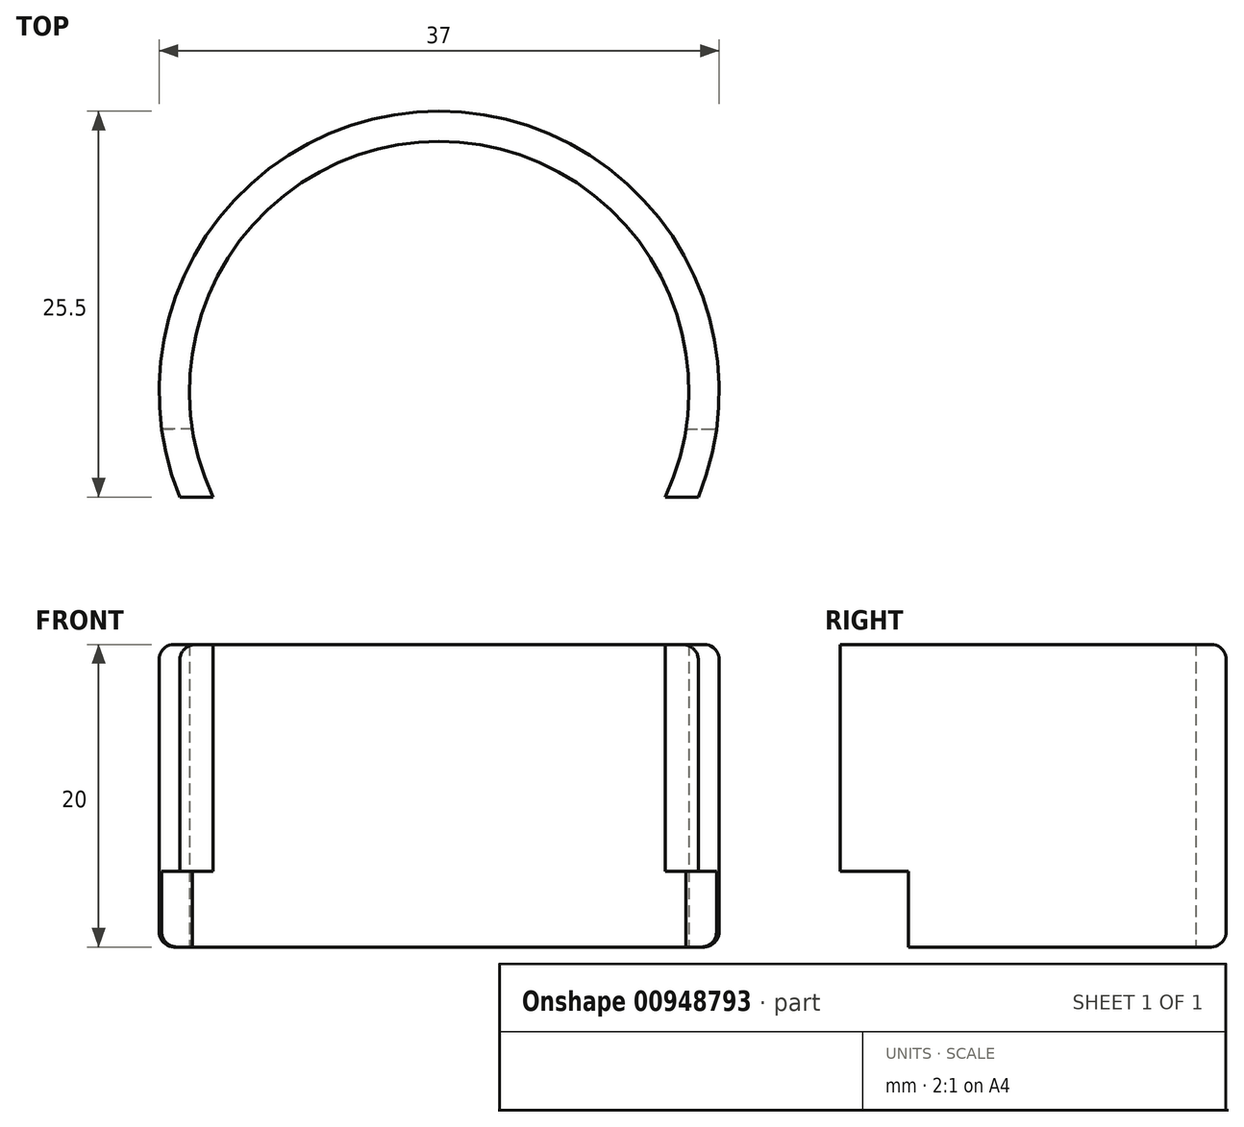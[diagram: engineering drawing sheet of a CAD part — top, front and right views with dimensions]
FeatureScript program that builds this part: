
annotation { "Feature Type Name" : "Feature", "Feature Type Description" : "" }
export const myFeature = defineFeature(function(context is Context, id is Id, definition is map)
    precondition{}
    {
        {
            var Q0;
            Q0=qCreatedBy(makeId("Top.planeOp"),FACE);
            var sketch = newSketch(context, id + "F0", { "sketchPlane" : qUnion([Q0])});
            skCircle(sketch, "E0", {"center": v(0, 0) * mm, "radius": 16.5 * mm});
            skCircle(sketch, "E1", {"center": v(0, 0) * mm, "radius": 18.5 * mm});
            skLineSegment(sketch, "E2", {"start": v(0, 0) * mm, "end": v(0, -7) * mm});
            skLineSegment(sketch, "E3", {"start": v(0, -7) * mm, "end": v(25.6, -7) * mm});
            skLineSegment(sketch, "E4", {"start": v(0, -7) * mm, "end": v(-26.93, -7) * mm});
            skPoint(sketch, "E5", {"position": v(0, -2.5) * mm});
            skLineSegment(sketch, "E6", {"start": v(0, -2.5) * mm, "end": v(27.78, -2.5) * mm});
            skLineSegment(sketch, "E7", {"start": v(0, -2.5) * mm, "end": v(-24.74, -2.5) * mm});
            skSolve(sketch);
        }
        {
            var Q0;
            {var subQ0=sQuery(id+"F0.wireOp",EDGE,"E7");var subQ1=sQuery(id+"F0.wireOp",EDGE,"E0");var subQ2=makeQuery(id+"F0.imprint","INTERSECT",VERTEX,{"derivedFrom":[subQ1,subQ0]});Q0=makeQuery(id+"F0.imprint","IMPRINT",FACE,{"disambiguationData":[TD([[makeQuery(id+"F0.imprint","IMPRINT",EDGE,{"disambiguationData":[TD([[subQ2,1.0]])],"derivedFrom":subQ1}),-1.0]])]});}
            var Q1;
            {var subQ0=sQuery(id+"F0.wireOp",EDGE,"E3");var subQ1=sQuery(id+"F0.wireOp",EDGE,"E0");var subQ2=makeQuery(id+"F0.imprint","INTERSECT",VERTEX,{"derivedFrom":[subQ1,subQ0]});Q1=makeQuery(id+"F0.imprint","IMPRINT",FACE,{"disambiguationData":[TD([[makeQuery(id+"F0.imprint","IMPRINT",EDGE,{"disambiguationData":[TD([[subQ2,-1.0]])],"derivedFrom":subQ1}),-1.0]])]});}
            var Q2;
            {var subQ0=sQuery(id+"F0.wireOp",EDGE,"E4");var subQ1=sQuery(id+"F0.wireOp",EDGE,"E0");var subQ2=makeQuery(id+"F0.imprint","INTERSECT",VERTEX,{"derivedFrom":[subQ1,subQ0]});Q2=makeQuery(id+"F0.imprint","IMPRINT",FACE,{"disambiguationData":[TD([[makeQuery(id+"F0.imprint","IMPRINT",EDGE,{"disambiguationData":[TD([[subQ2,1.0]])],"derivedFrom":subQ1}),-1.0]])]});}
            extrude(context, id + "F1", {"entities" : qUnion([Q0, Q1, Q2]), "depth" : 20 * mm, "offsetDistance" : 25 * mm});
        }
        {
            var Q0;
            {var subQ0=sQuery(id+"F0.wireOp",EDGE,"E4");var subQ1=sQuery(id+"F0.wireOp",EDGE,"E0");var subQ2=makeQuery(id+"F0.imprint","INTERSECT",VERTEX,{"derivedFrom":[subQ1,subQ0]});Q0=makeQuery(id+"F0.imprint","IMPRINT",FACE,{"disambiguationData":[TD([[makeQuery(id+"F0.imprint","IMPRINT",EDGE,{"disambiguationData":[TD([[subQ2,1.0]])],"derivedFrom":subQ1}),-1.0]])]});}
            var Q1;
            {var subQ0=sQuery(id+"F0.wireOp",EDGE,"E3");var subQ1=sQuery(id+"F0.wireOp",EDGE,"E0");var subQ2=makeQuery(id+"F0.imprint","INTERSECT",VERTEX,{"derivedFrom":[subQ1,subQ0]});Q1=makeQuery(id+"F0.imprint","IMPRINT",FACE,{"disambiguationData":[TD([[makeQuery(id+"F0.imprint","IMPRINT",EDGE,{"disambiguationData":[TD([[subQ2,-1.0]])],"derivedFrom":subQ1}),-1.0]])]});}
            extrude(context, id + "F2", {"entities" : qUnion([Q0, Q1]), "operationType" : NewBodyOperationType.REMOVE, "depth" : 5 * mm, "offsetDistance" : 25 * mm});
        }
        {
            var Q0;
            Q0=makeQuery(id+"F1.opExtrude","CAP_EDGE",EDGE,{"disambiguationData":[OSD([sQuery(id+"F0.wireOp",EDGE,"E1")])],"isStart":false});
            var Q1;
            Q1=makeQuery(id+"F1.opExtrude","CAP_EDGE",EDGE,{"disambiguationData":[OSD([sQuery(id+"F0.wireOp",EDGE,"E1")])],"isStart":true});
            fillet(context, id + "F3", {"entities" : qUnion([Q0, Q1]), "radius" : 1 * mm, "tangentPropagation" : true, "allowEdgeOverflow" : false});
        }
    });
